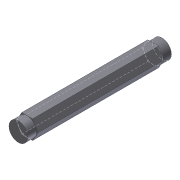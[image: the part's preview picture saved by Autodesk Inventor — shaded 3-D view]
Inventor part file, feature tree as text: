
AUTODESK INVENTOR PART (.ipt)
format: ipt  version: 2011 SP1 (Build 150282100, 282)  size: 88,576 bytes
history: native  units: in
note: dims shown in document units (in); Inventor stores cm internally (conversion verified against a paired STEP export)
features: extrude x3, sketch x3
ambient origin geometry x8: Origin, YZ Plane, XZ Plane, XY Plane, X Axis, Y Axis, Z Axis, Center Point
bodies: Solid1 (feature_tree)
feature tree (6):
  extrude  "Extrusion1"  Depth=2.48in TaperAngle=0.0deg
  extrude  "Extrusion2"  Depth=0.175in TaperAngle=0.0deg
  extrude  "Extrusion3"  Depth=0.175in TaperAngle=0.0deg
  sketch  "Sketch1"  dims[d0=0.373in d1=2.48in d2=0.0in]
  sketch  "Sketch2"  dims[d3=0.373in d4=0.175in d5=0.0in]
  sketch  "Sketch3"  dims[d6=0.373in d7=0.175in d8=0.0in]
